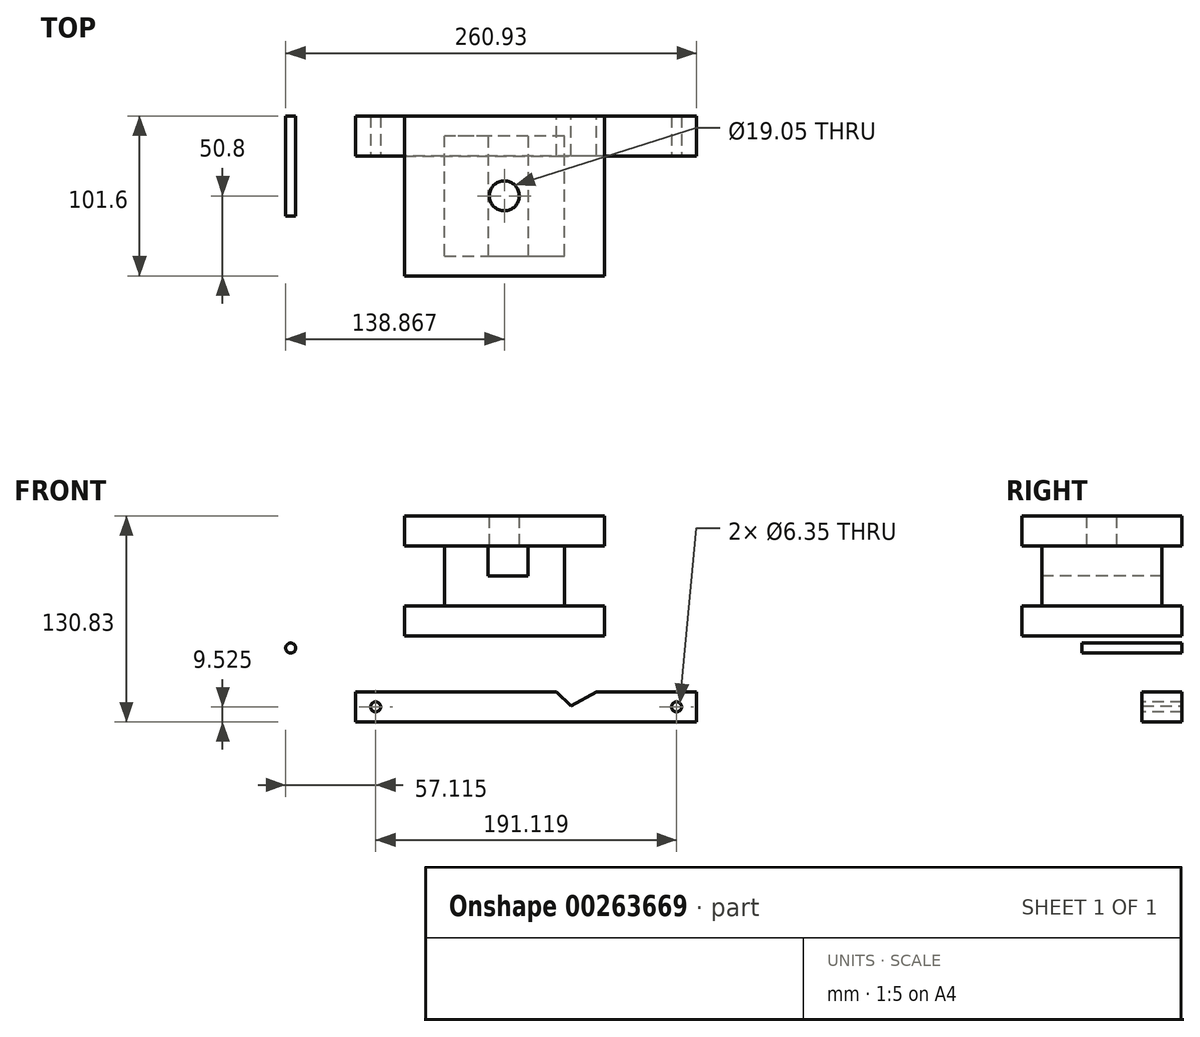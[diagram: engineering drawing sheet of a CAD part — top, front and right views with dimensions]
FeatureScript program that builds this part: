
annotation { "Feature Type Name" : "Feature", "Feature Type Description" : "" }
export const myFeature = defineFeature(function(context is Context, id is Id, definition is map)
    precondition{}
    {
        {
            var Q0;
            Q0=qCreatedBy(makeId("Front.planeOp"),FACE);
            var sketch = newSketch(context, id + "F0", { "sketchPlane" : qUnion([Q0])});
            skLineSegment(sketch, "E0", {"start": v(-68.4, 57.15) * mm, "end": v(58.6, 57.15) * mm});
            skLineSegment(sketch, "E1", {"start": v(58.6, 57.15) * mm, "end": v(58.6, 38.1) * mm});
            skPoint(sketch, "E2.end.orphan", {"position": v(-68.4, 0) * mm});
            skLineSegment(sketch, "E3", {"start": v(-68.4, 57.15) * mm, "end": v(-68.4, 38.1) * mm});
            skLineSegment(sketch, "E4", {"start": v(-68.4, 38.1) * mm, "end": v(-43, 38.1) * mm});
            skLineSegment(sketch, "E5", {"start": v(-43, 38.1) * mm, "end": v(-43, 0) * mm});
            skLineSegment(sketch, "E6", {"start": v(-43, 0) * mm, "end": v(-68.4, 0) * mm});
            skLineSegment(sketch, "E7", {"start": v(-68.4, 0) * mm, "end": v(-68.4, -19.05) * mm});
            skLineSegment(sketch, "E8", {"start": v(-68.4, -19.05) * mm, "end": v(58.6, -19.05) * mm});
            skLineSegment(sketch, "E9", {"start": v(58.6, -19.05) * mm, "end": v(58.6, 0) * mm});
            skLineSegment(sketch, "E10", {"start": v(58.6, 0) * mm, "end": v(33.2, 0) * mm});
            skLineSegment(sketch, "E11", {"start": v(33.2, 0) * mm, "end": v(33.2, 38.1) * mm});
            skLineSegment(sketch, "E12", {"start": v(33.2, 38.1) * mm, "end": v(58.6, 38.1) * mm});
            skLineSegment(sketch, "E13", {"start": v(-68.4, 38.1) * mm, "end": v(58.6, 38.1) * mm});
            skLineSegment(sketch, "E14", {"start": v(-68.4, 0) * mm, "end": v(58.6, 0) * mm});
            skSolve(sketch);
        }
        {
            var Q0;
            Q0=makeQuery(id+"F0.imprint","IMPRINT",FACE,{"disambiguationData":[TD([[makeQuery(id+"F0.imprint","IMPRINT",EDGE,{"derivedFrom":sQuery(id+"F0.wireOp",EDGE,"E0")}),-1.0]])]});
            var Q1;
            {var subQ2=sQuery(id+"F0.wireOp",EDGE,"E7");Q1=makeQuery(id+"F0.imprint","IMPRINT",FACE,{"disambiguationData":[TD([[makeQuery(id+"F0.imprint","IMPRINT",EDGE,{"derivedFrom":subQ2}),1.0]])]});}
            var Q2;
            {var subQ0=sQuery(id+"F0.wireOp",EDGE,"E5");Q2=makeQuery(id+"F0.imprint","IMPRINT",FACE,{"disambiguationData":[TD([[makeQuery(id+"F0.imprint","IMPRINT",EDGE,{"derivedFrom":subQ0}),1.0]])]});}
            extrude(context, id + "F1", {"entities" : qUnion([Q0, Q1, Q2]), "depth" : 101.6 * mm});
        }
        {
            var Q0;
            Q0=makeQuery(id+"F1.opExtrude","CAP_FACE",FACE,{"disambiguationData":[OSD([sQuery(id+"F0.wireOp",EDGE,"E0"),sQuery(id+"F0.wireOp",EDGE,"E1"),sQuery(id+"F0.wireOp",EDGE,"E3"),sQuery(id+"F0.wireOp",EDGE,"E5"),sQuery(id+"F0.wireOp",EDGE,"E7"),sQuery(id+"F0.wireOp",EDGE,"E8"),sQuery(id+"F0.wireOp",EDGE,"E9"),sQuery(id+"F0.wireOp",EDGE,"E11"),sQuery(id+"F0.wireOp",EDGE,"E13"),sQuery(id+"F0.wireOp",EDGE,"E14")])],"isStart":false});
            var sketch = newSketch(context, id + "F2", { "sketchPlane" : qUnion([Q0])});
            skLineSegment(sketch, "E15", {"start": v(-43, 38.1) * mm, "end": v(33.2, 38.1) * mm});
            skLineSegment(sketch, "E16", {"start": v(-43, 0) * mm, "end": v(33.2, 0) * mm});
            skSolve(sketch);
        }
        {
            var Q0;
            Q0=makeQuery(id+"F2.imprint","IMPRINT",FACE,{"disambiguationData":[TD([[makeQuery(id+"F2.imprint","IMPRINT",EDGE,{"derivedFrom":sQuery(id+"F2.wireOp",EDGE,"E15")}),-1.0]])]});
            extrude(context, id + "F3", {"entities" : qUnion([Q0]), "operationType" : NewBodyOperationType.REMOVE, "oppositeDirection" : true, "depth" : 12.7 * mm});
        }
        {
            var Q0;
            Q0=makeQuery(id+"F1.opExtrude","CAP_FACE",FACE,{"disambiguationData":[OSD([sQuery(id+"F0.wireOp",EDGE,"E0"),sQuery(id+"F0.wireOp",EDGE,"E1"),sQuery(id+"F0.wireOp",EDGE,"E3"),sQuery(id+"F0.wireOp",EDGE,"E5"),sQuery(id+"F0.wireOp",EDGE,"E7"),sQuery(id+"F0.wireOp",EDGE,"E8"),sQuery(id+"F0.wireOp",EDGE,"E9"),sQuery(id+"F0.wireOp",EDGE,"E11"),sQuery(id+"F0.wireOp",EDGE,"E13"),sQuery(id+"F0.wireOp",EDGE,"E14")])],"isStart":true});
            var sketch = newSketch(context, id + "F4", { "sketchPlane" : qUnion([Q0])});
            skLineSegment(sketch, "E17", {"start": v(-33.2, 38.1) * mm, "end": v(43, 38.1) * mm});
            skLineSegment(sketch, "E18", {"start": v(-33.2, 0) * mm, "end": v(43, 0) * mm});
            skSolve(sketch);
        }
        {
            var Q0;
            Q0=makeQuery(id+"F4.imprint","IMPRINT",FACE,{"disambiguationData":[TD([[makeQuery(id+"F4.imprint","IMPRINT",EDGE,{"derivedFrom":sQuery(id+"F4.wireOp",EDGE,"E17")}),-1.0]])]});
            extrude(context, id + "F5", {"entities" : qUnion([Q0]), "operationType" : NewBodyOperationType.REMOVE, "oppositeDirection" : true, "depth" : 12.7 * mm});
        }
        {
            var Q0;
            Q0=makeQuery(id+"F3.boolean.opBoolean","COPY",FACE,{"derivedFrom":makeQuery(id+"F3.opExtrude","CAP_FACE",FACE,{"disambiguationData":[OSD([sQuery(id+"F0.wireOp",EDGE,"E5"),sQuery(id+"F0.wireOp",EDGE,"E11"),sQuery(id+"F2.wireOp",EDGE,"E15"),sQuery(id+"F2.wireOp",EDGE,"E16")])],"isStart":false})});
            var sketch = newSketch(context, id + "F6", { "sketchPlane" : qUnion([Q0])});
            skLineSegment(sketch, "E19", {"start": v(-15.17, 38.1) * mm, "end": v(-15.17, 19.05) * mm});
            skLineSegment(sketch, "E20", {"start": v(-15.17, 19.05) * mm, "end": v(10.23, 19.05) * mm});
            skPoint(sketch, "E20.endSnap0", {"position": v(33.2, 19.05) * mm});
            skLineSegment(sketch, "E21", {"start": v(10.23, 19.05) * mm, "end": v(10.23, 38.1) * mm});
            skLineSegment(sketch, "E22", {"start": v(10.23, 38.1) * mm, "end": v(-15.17, 38.1) * mm});
            skSolve(sketch);
        }
        {
            var Q0;
            Q0=makeQuery(id+"F6.imprint","IMPRINT",FACE,{"disambiguationData":[TD([[makeQuery(id+"F6.imprint","IMPRINT",EDGE,{"derivedFrom":sQuery(id+"F6.wireOp",EDGE,"E19")}),1.0]])]});
            extrude(context, id + "F7", {"entities" : qUnion([Q0]), "operationType" : NewBodyOperationType.REMOVE, "endBound" : BoundingType.THROUGH_ALL, "oppositeDirection" : true, "depth" : 38.1 * mm});
        }
        {
            var Q0;
            Q0=makeQuery(id+"F1.opExtrude","SWEPT_FACE",FACE,{"disambiguationData":[OSD([sQuery(id+"F0.wireOp",EDGE,"E0")])]});
            var sketch = newSketch(context, id + "F8", { "sketchPlane" : qUnion([Q0])});
            skLineSegment(sketch, "E23", {"start": v(-4.9, -101.6) * mm, "end": v(-4.9, -50.8) * mm});
            skPoint(sketch, "E24.orphan", {"position": v(-68.4, -50.8) * mm});
            skPoint(sketch, "E25.orphan", {"position": v(-4.9, 0) * mm});
            skPoint(sketch, "E26.start.orphan", {"position": v(58.6, -50.8) * mm});
            skSolve(sketch);
        }
        {
            var Q0;
            Q0=sQuery(id+"F8.wireOp",VERTEX,"E23.end");
            var Q1;
            Q1=makeQuery(id+"F1.opExtrude","SWEPT_BODY",BODY,{"disambiguationData":[OSD([sQuery(id+"F0.wireOp",EDGE,"E0"),sQuery(id+"F0.wireOp",EDGE,"E1"),sQuery(id+"F0.wireOp",EDGE,"E3"),sQuery(id+"F0.wireOp",EDGE,"E5"),sQuery(id+"F0.wireOp",EDGE,"E7"),sQuery(id+"F0.wireOp",EDGE,"E8"),sQuery(id+"F0.wireOp",EDGE,"E9"),sQuery(id+"F0.wireOp",EDGE,"E11"),sQuery(id+"F0.wireOp",EDGE,"E13"),sQuery(id+"F0.wireOp",EDGE,"E14")])]});
            hole(context, id + "F9", {"style" : HoleStyle.SIMPLE, "endStyle" : HoleEndStyle.BLIND, "holeDiameter" : 19.05 * mm, "holeDepth" : 19.05 * mm, "tappedDepth" : 12.7 * mm, "tapClearance" : 3, "locations" : qUnion([Q0]), "scope" : qUnion([Q1])});
        }
        {
            var Q0;
            Q0=qCreatedBy(makeId("Front.planeOp"),FACE);
            var sketch = newSketch(context, id + "F10", { "sketchPlane" : qUnion([Q0])});
            skLineSegment(sketch, "E27", {"start": v(117.16, -54.63) * mm, "end": v(117.16, -73.68) * mm});
            skLineSegment(sketch, "E28", {"start": v(117.16, -73.68) * mm, "end": v(-99.35, -73.68) * mm});
            skPoint(sketch, "E29.start.orphan", {"position": v(-98.74, -54.63) * mm});
            skPoint(sketch, "E30.end.orphan", {"position": v(-99.35, -54.63) * mm});
            skLineSegment(sketch, "E31", {"start": v(-99.35, -73.68) * mm, "end": v(-99.35, -54.63) * mm});
            skLineSegment(sketch, "E32", {"start": v(-99.35, -54.63) * mm, "end": v(-98.74, -54.63) * mm});
            skLineSegment(sketch, "E33", {"start": v(117.16, -54.63) * mm, "end": v(53.66, -54.63) * mm});
            skLineSegment(sketch, "E34", {"start": v(-98.74, -54.63) * mm, "end": v(28.26, -54.63) * mm});
            skLineSegment(sketch, "E35", {"start": v(28.26, -54.63) * mm, "end": v(37.34, -63.5) * mm});
            skLineSegment(sketch, "E36", {"start": v(53.66, -54.63) * mm, "end": v(37.34, -63.5) * mm});
            skPoint(sketch, "E37.start.orphan", {"position": v(-99.35, -64.15) * mm});
            skSolve(sketch);
        }
        {
            var Q0;
            Q0=makeQuery(id+"F10.imprint","IMPRINT",FACE,{"disambiguationData":[TD([[makeQuery(id+"F10.imprint","IMPRINT",EDGE,{"derivedFrom":sQuery(id+"F10.wireOp",EDGE,"E27")}),-1.0]])]});
            extrude(context, id + "F11", {"entities" : qUnion([Q0]), "depth" : 25.4 * mm});
        }
        {
            var Q0;
            Q0=makeQuery(id+"F11.opExtrude","CAP_FACE",FACE,{"disambiguationData":[OSD([sQuery(id+"F10.wireOp",EDGE,"E27"),sQuery(id+"F10.wireOp",EDGE,"E28"),sQuery(id+"F10.wireOp",EDGE,"E31"),sQuery(id+"F10.wireOp",EDGE,"E32"),sQuery(id+"F10.wireOp",EDGE,"E33"),sQuery(id+"F10.wireOp",EDGE,"E34"),sQuery(id+"F10.wireOp",EDGE,"E35"),sQuery(id+"F10.wireOp",EDGE,"E36")])],"isStart":false});
            var sketch = newSketch(context, id + "F12", { "sketchPlane" : qUnion([Q0])});
            skLineSegment(sketch, "E38", {"start": v(117.16, -73.68) * mm, "end": v(117.16, -64.15) * mm});
            skLineSegment(sketch, "E39", {"start": v(117.16, -64.15) * mm, "end": v(104.46, -64.15) * mm});
            skLineSegment(sketch, "E40", {"start": v(-99.35, -73.68) * mm, "end": v(-99.35, -64.15) * mm});
            skLineSegment(sketch, "E41", {"start": v(-99.35, -64.15) * mm, "end": v(-86.65, -64.15) * mm});
            skSolve(sketch);
        }
        {
            var Q0;
            Q0=sQuery(id+"F12.wireOp",VERTEX,"E41.end");
            var Q1;
            Q1=sQuery(id+"F12.wireOp",VERTEX,"E39.end");
            var Q2;
            Q2=makeQuery(id+"F11.opExtrude","SWEPT_BODY",BODY,{"disambiguationData":[OSD([sQuery(id+"F10.wireOp",EDGE,"E27"),sQuery(id+"F10.wireOp",EDGE,"E28"),sQuery(id+"F10.wireOp",EDGE,"E31"),sQuery(id+"F10.wireOp",EDGE,"E32"),sQuery(id+"F10.wireOp",EDGE,"E33"),sQuery(id+"F10.wireOp",EDGE,"E34"),sQuery(id+"F10.wireOp",EDGE,"E35"),sQuery(id+"F10.wireOp",EDGE,"E36")])]});
            hole(context, id + "F13", {"style" : HoleStyle.SIMPLE, "endStyle" : HoleEndStyle.THROUGH, "holeDiameter" : 6.35 * mm, "tappedDepth" : 12.7 * mm, "tapClearance" : 3, "locations" : qUnion([Q0, Q1]), "scope" : qUnion([Q2])});
        }
        {
            var Q0;
            Q0=qCreatedBy(makeId("Front.planeOp"),FACE);
            var sketch = newSketch(context, id + "F14", { "sketchPlane" : qUnion([Q0])});
            skCircle(sketch, "E42", {"center": v(-140.6, -26.77) * mm, "radius": 3.18 * mm});
            skSolve(sketch);
        }
        {
            var Q0;
            Q0=makeQuery(id+"F14.imprint","IMPRINT",FACE,{"disambiguationData":[TD([[makeQuery(id+"F14.imprint","IMPRINT",EDGE,{"derivedFrom":sQuery(id+"F14.wireOp",EDGE,"E42")}),1.0]])]});
            extrude(context, id + "F15", {"entities" : qUnion([Q0]), "depth" : 63.5 * mm});
        }
    });
